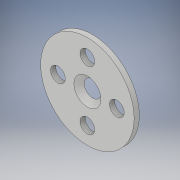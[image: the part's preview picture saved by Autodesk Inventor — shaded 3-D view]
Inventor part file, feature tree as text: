
AUTODESK INVENTOR PART (.ipt)
format: ipt  version: 2019.4 (Build 234330000, 330)  size: 120,320 bytes
history: native  units: in
note: dims shown in document units (in); Inventor stores cm internally (conversion verified against a paired STEP export)
features: sketch x3, extrude x2, hole x1, chamfer x1
ambient origin geometry x8: Origin, YZ Plane, XZ Plane, XY Plane, X Axis, Y Axis, Z Axis, Center Point
bodies: Solid1 (feature_tree)
feature tree (7):
  extrude  "Extrusion1"  Depth=0.0625in TaperAngle=0.0deg
  hole  "Hole1"  [1 undecoded]
  extrude  "Extrusion2"  Depth=0.0625in
  chamfer  "Chamfer1"  Distance=0.2in
  sketch  "Sketch1"  dims[d0=1.125in d1=0.0625in d2=0.0in]
  sketch  "Sketch2"  dims[d3=0.355in d4=0.355in]
  sketch  "Sketch3"  dims[d5=0.355in d6=0.355in d7=0.177in d8=0.328in d9=0.332in d10=0.25in d11=0.5635in d12=0.484in d13=0.8108in d14=0.2in d15=0.0625in d16=0.0in d17=0.0625in d18=0.125in d19=45.0deg]
note: 1 required parameter value undecoded (feature->parameter linkage not recoverable at this tier; creation-order binding heuristic only, values carry confidence <= 0.55)
